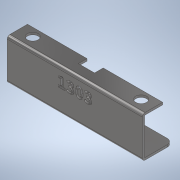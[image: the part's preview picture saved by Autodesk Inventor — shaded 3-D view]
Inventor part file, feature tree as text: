
AUTODESK INVENTOR PART (.ipt)
format: ipt  version: 2020 (Build 240168000, 168)  size: 545,792 bytes
history: native  units: mm
features: other x4, extrude x3, fillet x1, sketch x1, projected_geometry x1
ambient origin geometry x8: Origin, YZ Plane, XZ Plane, XY Plane, X Axis, Y Axis, Z Axis, Center Point
bodies: Body1 (feature_tree)
feature tree (10):
  other  "實體1"
  extrude  "擠出1"  Depth=124.7mm
  extrude  "擠出3"  Depth=26.3mm
  extrude  "擠出4"  Depth=33.0mm
  other  "折彎零件1"
  other  "折彎零件2"
  fillet  "圓角1"  Radius=17.0mm
  sketch  "草圖4"
  projected_geometry  "投影迴路1"
  other  "定義1"
